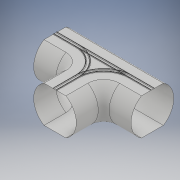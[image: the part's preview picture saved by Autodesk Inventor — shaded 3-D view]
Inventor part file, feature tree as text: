
AUTODESK INVENTOR PART (.ipt)
format: ipt  version: 2017 (Build 210142000, 142)  size: 434,688 bytes
history: native  units: in
note: dims shown in document units (in); Inventor stores cm internally (conversion verified against a paired STEP export)
features: sketch x7, extrude x4, sweep x2, plane x1, mirror x1, delete_face x1
ambient origin geometry x8: Origin, YZ Plane, XZ Plane, XY Plane, X Axis, Y Axis, Z Axis, Center Point
bodies: Solid1 (feature_tree)
feature tree (16):
  sketch  "Sketch1"  dims[d0=6.6667in d2=9.7746in d3=4.0in d4=0.0in d5=-4.8873in]
  extrude  "corridor"  [1 undecoded]
  plane  "Work Plane1"
  sketch  "Sketch4"  dims[d6=6.6667in d10=4.0in d11=0.0in d20=0.0in d21=0.0in]
  extrude  "T bottom"  TaperAngle=0.0deg  [1 undecoded]
  sketch  "Sketch8"  dims[d171=4.8873in]
  sketch  "Sketch7"  dims[d22=4.8873in d23=0.0in]
  sweep  "corner curve"
  sketch  "Sketch9"  dims[d187=4.0in d188=0.5833in d189=3.8873in d190=3.8873in d191=1.7083in d192=0.0625in d193=0.0625in d194=1.6458in d195=0.25in d196=0.125in d198=0.0884in d199=45.0deg d200=3.3333in d201=0.125in]
  extrude  "flat of T"  TaperAngle=0.0deg  [1 undecoded]
  mirror  "Mirror parts"
  sweep  "corner curve 2"
  extrude  "hole fill in"  [1 undecoded]
  delete_face  "Delete Face1"
  sketch  "Sketch17"  dims[d202=4.0in d203=0.5833in d204=3.8873in d205=3.8873in d206=1.7083in d207=0.0625in d208=0.0625in d209=1.6458in d210=0.25in d211=0.125in d213=0.0884in d214=45.0deg d215=3.3333in d216=0.125in d217=0.0in d218=0.0in]
  sketch  "Sketch19"  dims[d219=1.0in d220=0.0in]
note: 4 required parameter values undecoded (feature->parameter linkage not recoverable at this tier; creation-order binding heuristic only, values carry confidence <= 0.55)
